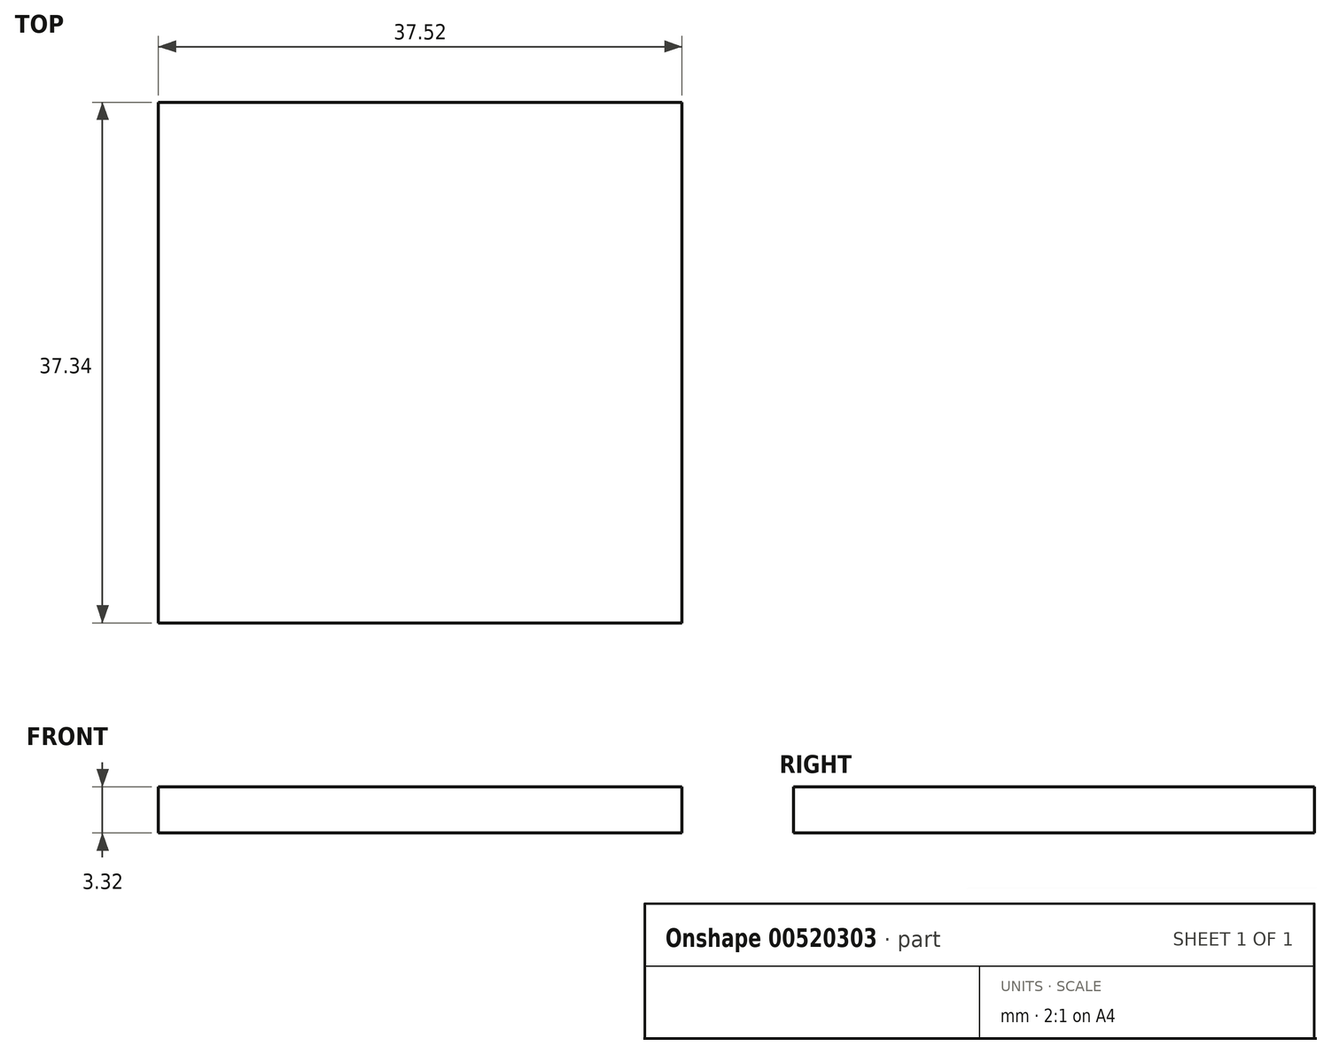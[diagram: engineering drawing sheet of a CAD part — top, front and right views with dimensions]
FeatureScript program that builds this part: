
annotation { "Feature Type Name" : "Feature", "Feature Type Description" : "" }
export const myFeature = defineFeature(function(context is Context, id is Id, definition is map)
    precondition{}
    {
        {
            var Q0;
            Q0=qCreatedBy(makeId("Front.planeOp"),FACE);
            var sketch = newSketch(context, id + "F0", { "sketchPlane" : qUnion([Q0])});
            skLineSegment(sketch, "E0.bottom", {"start": v(18.76, -1.66) * mm, "end": v(-18.76, -1.66) * mm});
            skLineSegment(sketch, "E0.top", {"start": v(18.76, 1.66) * mm, "end": v(-18.76, 1.66) * mm});
            skLineSegment(sketch, "E0.left", {"start": v(18.76, -1.66) * mm, "end": v(18.76, 1.66) * mm});
            skLineSegment(sketch, "E0.right", {"start": v(-18.76, -1.66) * mm, "end": v(-18.76, 1.66) * mm});
            skPoint(sketch, "E0.middle", {"position": v(0, 0) * mm});
            skSolve(sketch);
        }
        {
            var Q0;
            Q0 = qSketchRegion(id + "F0", true);
            extrude(context, id + "F1", {"entities" : qUnion([Q0]), "depth" : 37.34 * mm, "offsetDistance" : 25.4 * mm});
        }
    });
